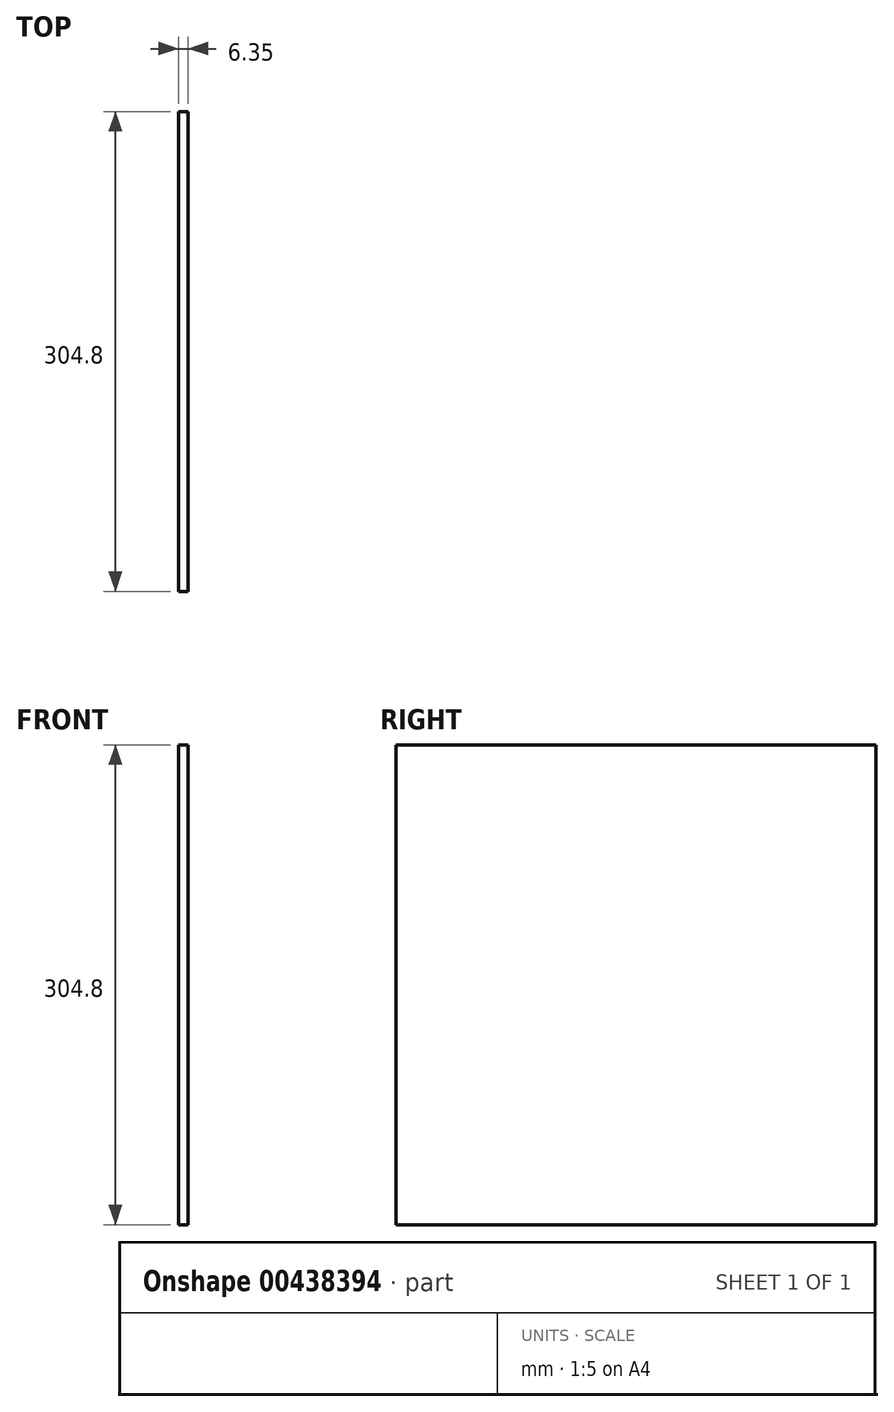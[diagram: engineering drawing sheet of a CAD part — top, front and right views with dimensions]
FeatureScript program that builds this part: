
annotation { "Feature Type Name" : "Feature", "Feature Type Description" : "" }
export const myFeature = defineFeature(function(context is Context, id is Id, definition is map)
    precondition{}
    {
        {
            var Q0;
            Q0=qCreatedBy(makeId("Front.planeOp"),FACE);
            var sketch = newSketch(context, id + "F0", { "sketchPlane" : qUnion([Q0])});
            skLineSegment(sketch, "E0.bottom", {"start": v(-47.16, 272) * mm, "end": v(-40.8, 272) * mm});
            skLineSegment(sketch, "E0.top", {"start": v(-47.16, -32.8) * mm, "end": v(-40.8, -32.8) * mm});
            skLineSegment(sketch, "E0.left", {"start": v(-47.16, 272) * mm, "end": v(-47.16, -32.8) * mm});
            skLineSegment(sketch, "E0.right", {"start": v(-40.8, 272) * mm, "end": v(-40.8, -32.8) * mm});
            skSolve(sketch);
        }
        {
            var Q0;
            Q0=makeQuery(id+"F0.imprint","IMPRINT",FACE,{"disambiguationData":[TD([[makeQuery(id+"F0.imprint","IMPRINT",EDGE,{"derivedFrom":sQuery(id+"F0.wireOp",EDGE,"E0.bottom")}),-1.0]])]});
            extrude(context, id + "F1", {"entities" : qUnion([Q0]), "depth" : 304.8 * mm});
        }
    });
